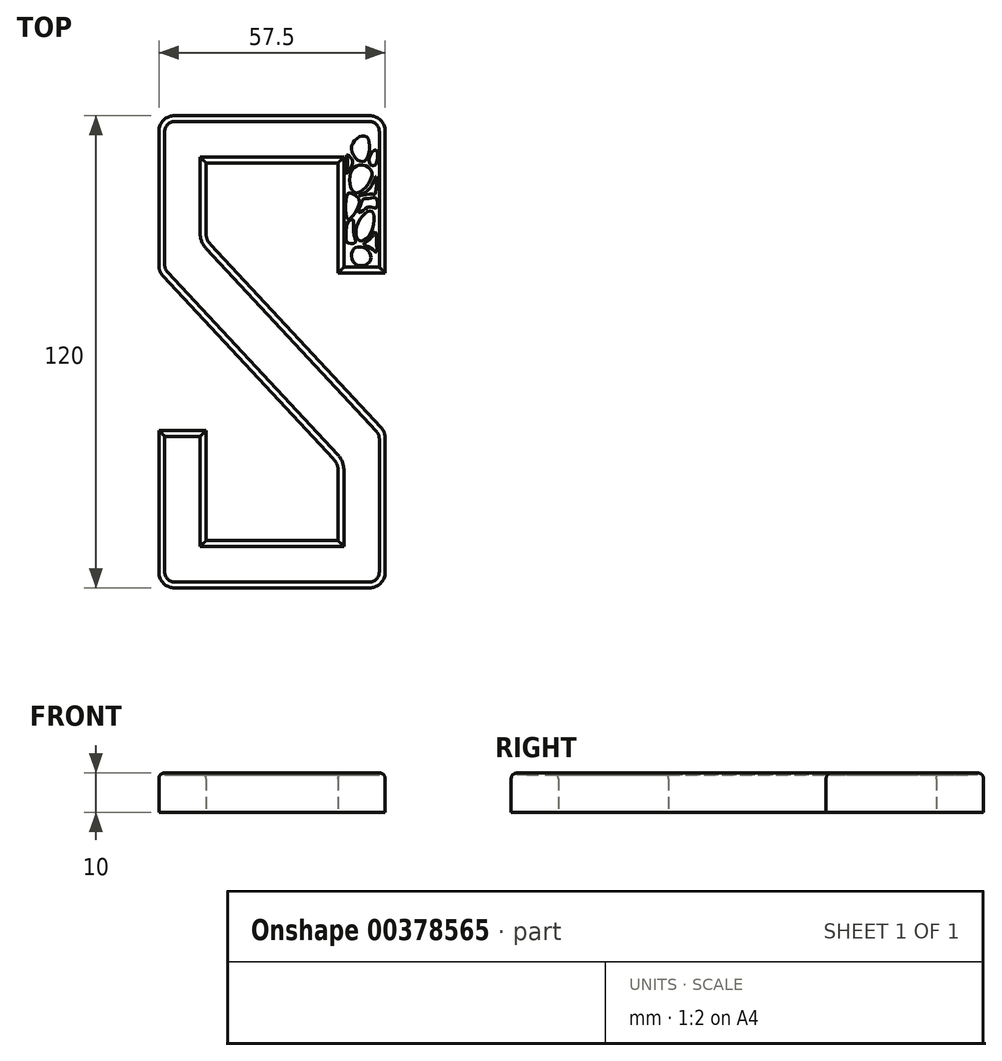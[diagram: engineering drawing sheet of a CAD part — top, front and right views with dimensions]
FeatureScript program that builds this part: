
annotation { "Feature Type Name" : "Feature", "Feature Type Description" : "" }
export const myFeature = defineFeature(function(context is Context, id is Id, definition is map)
    precondition{}
    {
        {
            var Q0;
            Q0=qCreatedBy(makeId("Top.planeOp"),FACE);
            var sketch = newSketch(context, id + "F0", { "sketchPlane" : qUnion([Q0])});
            skLineSegment(sketch, "E0.bottom", {"start": v(4, 0) * mm, "end": v(53.5, 0) * mm});
            skLineSegment(sketch, "E0.top", {"start": v(4, 120) * mm, "end": v(53.5, 120) * mm});
            skLineSegment(sketch, "E0.left", {"start": v(0, 4) * mm, "end": v(0, 40) * mm});
            skLineSegment(sketch, "E0.right", {"start": v(57.5, 4) * mm, "end": v(57.5, 38.02) * mm});
            skLineSegment(sketch, "E1", {"start": v(0, 40) * mm, "end": v(12, 40) * mm});
            skLineSegment(sketch, "E2.0", {"start": v(12, 108) * mm, "end": v(45.5, 108) * mm});
            skLineSegment(sketch, "E2.1", {"start": v(12, 12) * mm, "end": v(12, 40) * mm});
            skLineSegment(sketch, "E2.2", {"start": v(12, 12) * mm, "end": v(45.5, 12) * mm});
            skLineSegment(sketch, "E2.3", {"start": v(45.5, 12) * mm, "end": v(45.5, 29.98) * mm});
            skLineSegment(sketch, "E3", {"start": v(1.07, 79.25) * mm, "end": v(44.43, 32.7) * mm});
            skLineSegment(sketch, "E4", {"start": v(56.43, 40.75) * mm, "end": v(13.07, 87.3) * mm});
            skLineSegment(sketch, "E5.trimOffspring", {"start": v(45.5, 80) * mm, "end": v(57.5, 80) * mm});
            skLineSegment(sketch, "E6.trimOffspring", {"start": v(45.5, 80) * mm, "end": v(45.5, 108) * mm});
            skLineSegment(sketch, "E7.trimOffspring", {"start": v(57.5, 80) * mm, "end": v(57.5, 116) * mm});
            skLineSegment(sketch, "E8.trimOffspring", {"start": v(12, 90.02) * mm, "end": v(12, 108) * mm});
            skLineSegment(sketch, "E9.trimOffspring", {"start": v(0, 81.98) * mm, "end": v(0, 116) * mm});
            skPoint(sketch, "E10.visualSharp", {"position": v(57.5, 120) * mm});
            skArc(sketch, "E10.filletArc", {"start": v(57.5, 116) * mm, "mid": v(56.33, 118.83) * mm, "end": v(53.5, 120) * mm});
            skPoint(sketch, "E11.visualSharp", {"position": v(0, 120) * mm});
            skArc(sketch, "E11.filletArc", {"start": v(4, 120) * mm, "mid": v(1.17, 118.83) * mm, "end": v(0, 116) * mm});
            skPoint(sketch, "E12.visualSharp", {"position": v(0, 80.4) * mm});
            skArc(sketch, "E12.filletArc", {"start": v(0, 81.98) * mm, "mid": v(0.28, 80.51) * mm, "end": v(1.07, 79.25) * mm});
            skPoint(sketch, "E13.visualSharp", {"position": v(12, 88.45) * mm});
            skArc(sketch, "E13.filletArc", {"start": v(12, 90.02) * mm, "mid": v(12.28, 88.56) * mm, "end": v(13.07, 87.3) * mm});
            skPoint(sketch, "E14.visualSharp", {"position": v(57.5, 0) * mm});
            skArc(sketch, "E14.filletArc", {"start": v(53.5, 0) * mm, "mid": v(56.33, 1.17) * mm, "end": v(57.5, 4) * mm});
            skPoint(sketch, "E15.visualSharp", {"position": v(0, 0) * mm});
            skArc(sketch, "E15.filletArc", {"start": v(0, 4) * mm, "mid": v(1.17, 1.17) * mm, "end": v(4, 0) * mm});
            skPoint(sketch, "E16.visualSharp", {"position": v(45.5, 31.55) * mm});
            skArc(sketch, "E16.filletArc", {"start": v(45.5, 29.98) * mm, "mid": v(45.22, 31.44) * mm, "end": v(44.43, 32.7) * mm});
            skPoint(sketch, "E17.visualSharp", {"position": v(57.5, 39.6) * mm});
            skArc(sketch, "E17.filletArc", {"start": v(57.5, 38.02) * mm, "mid": v(57.22, 39.48) * mm, "end": v(56.43, 40.75) * mm});
            skSolve(sketch);
        }
        {
            var Q0;
            Q0 = qSketchRegion(id + "F0", true);
            extrude(context, id + "F1", {"entities" : qUnion([Q0]), "depth" : 10 * mm});
        }
        {
            var Q0;
            Q0=makeQuery(id+"F1.opExtrude","CAP_FACE",FACE,{"disambiguationData":[OSD([sQuery(id+"F0.wireOp",EDGE,"E0.bottom"),sQuery(id+"F0.wireOp",EDGE,"E0.top"),sQuery(id+"F0.wireOp",EDGE,"E0.left"),sQuery(id+"F0.wireOp",EDGE,"E0.right"),sQuery(id+"F0.wireOp",EDGE,"E1"),sQuery(id+"F0.wireOp",EDGE,"E2.0"),sQuery(id+"F0.wireOp",EDGE,"E2.1"),sQuery(id+"F0.wireOp",EDGE,"E2.2"),sQuery(id+"F0.wireOp",EDGE,"E2.3"),sQuery(id+"F0.wireOp",EDGE,"E3"),sQuery(id+"F0.wireOp",EDGE,"E4"),sQuery(id+"F0.wireOp",EDGE,"E5.trimOffspring"),sQuery(id+"F0.wireOp",EDGE,"E6.trimOffspring"),sQuery(id+"F0.wireOp",EDGE,"E7.trimOffspring"),sQuery(id+"F0.wireOp",EDGE,"E8.trimOffspring"),sQuery(id+"F0.wireOp",EDGE,"E9.trimOffspring"),sQuery(id+"F0.wireOp",EDGE,"E10.filletArc"),sQuery(id+"F0.wireOp",EDGE,"E11.filletArc"),sQuery(id+"F0.wireOp",EDGE,"E12.filletArc"),sQuery(id+"F0.wireOp",EDGE,"E13.filletArc"),sQuery(id+"F0.wireOp",EDGE,"E14.filletArc"),sQuery(id+"F0.wireOp",EDGE,"E15.filletArc"),sQuery(id+"F0.wireOp",EDGE,"E16.filletArc"),sQuery(id+"F0.wireOp",EDGE,"E17.filletArc")])],"isStart":false});
            fillet(context, id + "F2", {"entities" : qUnion([Q0]), "radius" : 1.5 * mm, "tangentPropagation" : true, "allowEdgeOverflow" : false});
        }
        {
            var Q0;
            Q0=makeQuery(id+"F1.opExtrude","CAP_FACE",FACE,{"disambiguationData":[OSD([sQuery(id+"F0.wireOp",EDGE,"E0.bottom"),sQuery(id+"F0.wireOp",EDGE,"E0.top"),sQuery(id+"F0.wireOp",EDGE,"E0.left"),sQuery(id+"F0.wireOp",EDGE,"E0.right"),sQuery(id+"F0.wireOp",EDGE,"E1"),sQuery(id+"F0.wireOp",EDGE,"E2.0"),sQuery(id+"F0.wireOp",EDGE,"E2.1"),sQuery(id+"F0.wireOp",EDGE,"E2.2"),sQuery(id+"F0.wireOp",EDGE,"E2.3"),sQuery(id+"F0.wireOp",EDGE,"E3"),sQuery(id+"F0.wireOp",EDGE,"E4"),sQuery(id+"F0.wireOp",EDGE,"E5.trimOffspring"),sQuery(id+"F0.wireOp",EDGE,"E6.trimOffspring"),sQuery(id+"F0.wireOp",EDGE,"E7.trimOffspring"),sQuery(id+"F0.wireOp",EDGE,"E8.trimOffspring"),sQuery(id+"F0.wireOp",EDGE,"E9.trimOffspring"),sQuery(id+"F0.wireOp",EDGE,"E10.filletArc"),sQuery(id+"F0.wireOp",EDGE,"E11.filletArc"),sQuery(id+"F0.wireOp",EDGE,"E12.filletArc"),sQuery(id+"F0.wireOp",EDGE,"E13.filletArc"),sQuery(id+"F0.wireOp",EDGE,"E14.filletArc"),sQuery(id+"F0.wireOp",EDGE,"E15.filletArc"),sQuery(id+"F0.wireOp",EDGE,"E16.filletArc"),sQuery(id+"F0.wireOp",EDGE,"E17.filletArc")])],"isStart":false});
            var sketch = newSketch(context, id + "F3", { "sketchPlane" : qUnion([Q0])});
            skFitSpline(sketch, "E18", {"points": [v(52.82, 114.56) * mm, v(52.06, 108.4) * mm, v(48.97, 112.12) * mm, v(52.82, 114.56) * mm]});
            skFitSpline(sketch, "E19", {"points": [v(50.87, 107.44) * mm, v(48.48, 104.27) * mm, v(50.15, 100.37) * mm, v(54.14, 105.34) * mm, v(50.87, 107.44) * mm]});
            skFitSpline(sketch, "E20", {"points": [v(55.18, 111.22) * mm, v(53.43, 108.44) * mm, v(54.94, 107.44) * mm, v(55.18, 111.22) * mm]});
            skFitSpline(sketch, "E21", {"points": [v(47.7, 110.04) * mm, v(49.23, 108.35) * mm, v(47.61, 105.34) * mm, v(47.95, 108.3) * mm, v(47.7, 110.04) * mm]});
            skFitSpline(sketch, "E22", {"points": [v(55.18, 104.54) * mm, v(53.63, 101.63) * mm, v(50.87, 99.67) * mm, v(54.14, 100.1) * mm, v(54.94, 100.1) * mm, v(55.18, 104.54) * mm]});
            skFitSpline(sketch, "E23", {"points": [v(47.95, 100.1) * mm, v(47.95, 93.8) * mm, v(49.8, 95.24) * mm, v(50.87, 98.67) * mm, v(48.87, 100.23) * mm, v(47.95, 100.1) * mm]});
            skFitSpline(sketch, "E24", {"points": [v(54.14, 95.64) * mm, v(50.81, 93.2) * mm, v(50.7, 88.38) * mm, v(53.53, 89.61) * mm, v(54.14, 95.64) * mm]});
            skFitSpline(sketch, "E25", {"points": [v(51.96, 98.76) * mm, v(50.87, 95.33) * mm, v(53.2, 96.77) * mm, v(55.18, 96.56) * mm, v(55.18, 98.99) * mm, v(53.16, 98.9) * mm, v(51.96, 98.76) * mm]});
            skFitSpline(sketch, "E26", {"points": [v(49.5, 86.14) * mm, v(53.06, 85.83) * mm, v(53.4, 82.67) * mm, v(49.75, 82.49) * mm, v(49.5, 86.14) * mm]});
            skFitSpline(sketch, "E27", {"points": [v(54.94, 90.44) * mm, v(53.49, 88.48) * mm, v(52.08, 87.4) * mm, v(54.14, 86.14) * mm, v(55.18, 85.3) * mm, v(55.35, 87.41) * mm, v(54.94, 90.44) * mm]});
            skFitSpline(sketch, "E28", {"points": [v(49.5, 92.47) * mm, v(49.5, 89.75) * mm, v(49.88, 87.77) * mm, v(47.95, 87.69) * mm, v(47.61, 89.64) * mm, v(47.95, 92.85) * mm, v(49.2, 93.5) * mm, v(49.5, 92.47) * mm]});
            skFitSpline(sketch, "E29", {"points": [v(47.85, 86.74) * mm, v(48.8, 86.21) * mm, v(48.2, 83.86) * mm, v(47.95, 82.26) * mm, v(47.48, 82.22) * mm, v(47.48, 82.22) * mm, v(47.29, 84.56) * mm, v(47.85, 86.74) * mm]});
            skSolve(sketch);
        }
        {
            var Q0;
            Q0=makeQuery(id+"F3.imprint","IMPRINT",FACE,{"disambiguationData":[TD([[makeQuery(id+"F3.imprint","IMPRINT",EDGE,{"derivedFrom":sQuery(id+"F3.wireOp",EDGE,"E18")}),1.0]])]});
            extrude(context, id + "F4", {"entities" : qUnion([Q0]), "operationType" : NewBodyOperationType.REMOVE, "oppositeDirection" : true, "depth" : 0.5 * mm});
        }
    });
